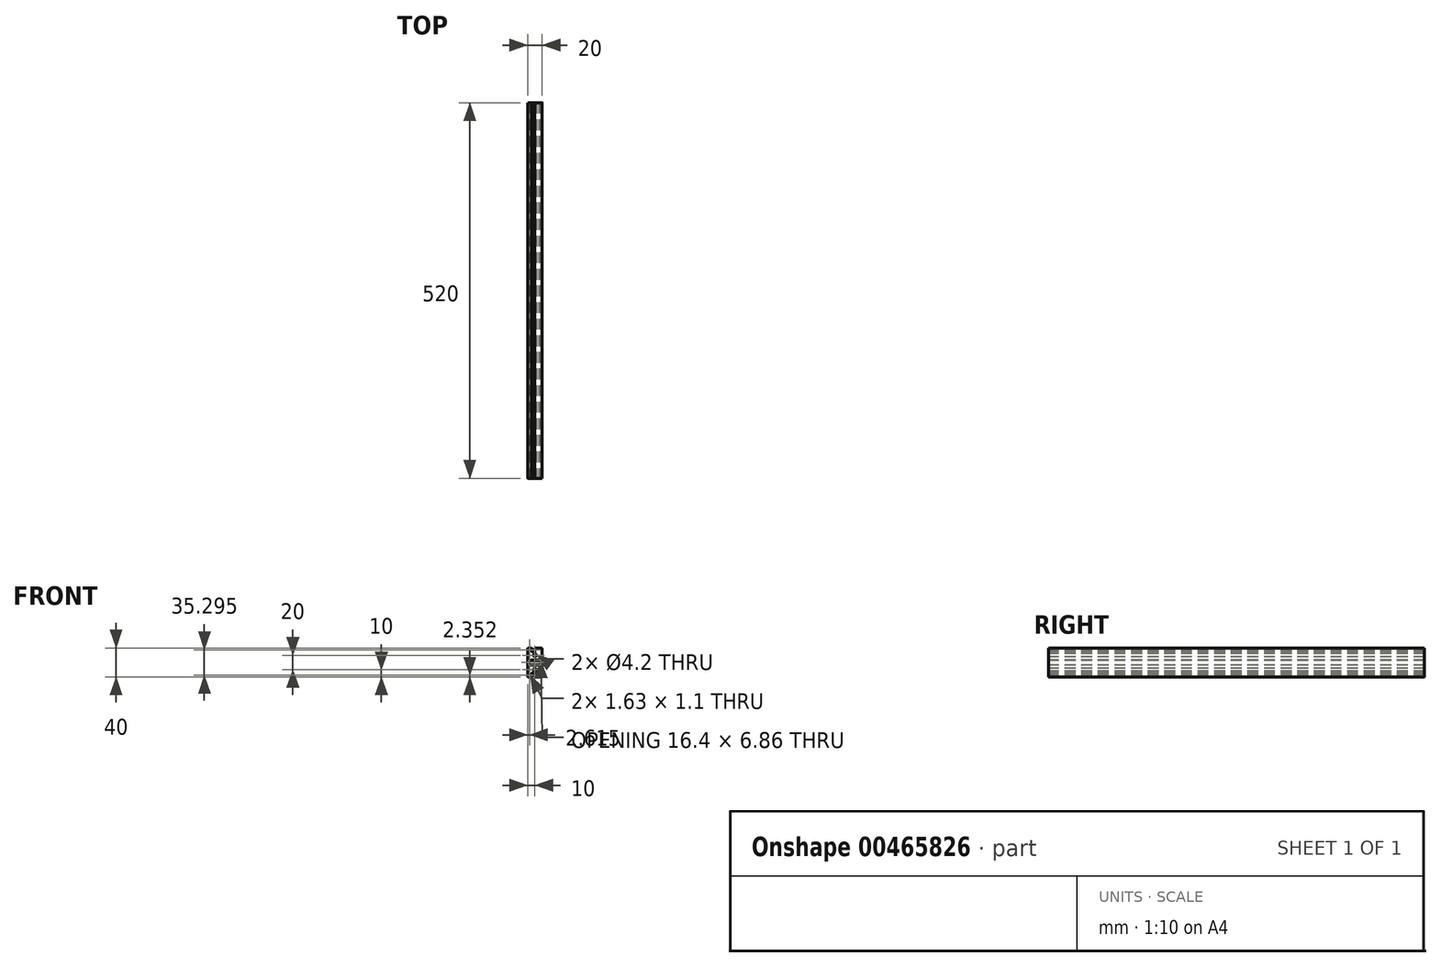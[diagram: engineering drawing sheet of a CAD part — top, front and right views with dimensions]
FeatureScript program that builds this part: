
annotation { "Feature Type Name" : "Feature", "Feature Type Description" : "" }
export const myFeature = defineFeature(function(context is Context, id is Id, definition is map)
    precondition{}
    {
        {
            var Q0;
            Q0=qCreatedBy(makeId("Front.planeOp"),FACE);
            var sketch = newSketch(context, id + "F0", { "sketchPlane" : qUnion([Q0])});
            skLineSegment(sketch, "E0.bottom", {"start": v(10, 10) * mm, "end": v(-10, 10) * mm});
            skLineSegment(sketch, "E0.top", {"start": v(10, -10) * mm, "end": v(-10, -10) * mm});
            skLineSegment(sketch, "E0.left", {"start": v(10, 10) * mm, "end": v(10, -10) * mm});
            skLineSegment(sketch, "E0.right", {"start": v(-10, 10) * mm, "end": v(-10, -10) * mm});
            skPoint(sketch, "E0.middle", {"position": v(0, 0) * mm});
            skSolve(sketch);
        }
        {
            var Q0;
            Q0=qSketchRegion(id+"F0",true);
            extrude(context, id + "F1", {"entities" : qUnion([Q0]), "depth" : 520 * mm});
        }
        {
            var Q0;
            Q0=makeQuery(id+"F1.opExtrude","CAP_FACE",FACE,{"disambiguationData":[OSD([sQuery(id+"F0.wireOp",EDGE,"E0.bottom"),sQuery(id+"F0.wireOp",EDGE,"E0.top"),sQuery(id+"F0.wireOp",EDGE,"E0.left"),sQuery(id+"F0.wireOp",EDGE,"E0.right")])],"isStart":false});
            var sketch = newSketch(context, id + "F2", { "sketchPlane" : qUnion([Q0])});
            skCircle(sketch, "E1", {"center": v(0, 0) * mm, "radius": 2.1 * mm});
            skSolve(sketch);
        }
        {
            var Q0;
            Q0=qSketchRegion(id+"F2",true);
            extrude(context, id + "F3", {"entities" : qUnion([Q0]), "operationType" : NewBodyOperationType.REMOVE, "endBound" : BoundingType.THROUGH_ALL, "oppositeDirection" : true, "depth" : 25 * mm});
        }
        {
            var Q0;
            Q0=makeQuery(id+"F1.opExtrude","SWEPT_EDGE",EDGE,{"disambiguationData":[OSD([sQuery(id+"F0.wireOp",EDGE,"E0.bottom"),sQuery(id+"F0.wireOp",EDGE,"E0.right")])]});
            var Q1;
            Q1=makeQuery(id+"F1.opExtrude","SWEPT_EDGE",EDGE,{"disambiguationData":[OSD([sQuery(id+"F0.wireOp",EDGE,"E0.bottom"),sQuery(id+"F0.wireOp",EDGE,"E0.left")])]});
            var Q2;
            Q2=makeQuery(id+"F1.opExtrude","SWEPT_EDGE",EDGE,{"disambiguationData":[OSD([sQuery(id+"F0.wireOp",EDGE,"E0.top"),sQuery(id+"F0.wireOp",EDGE,"E0.left")])]});
            var Q3;
            Q3=makeQuery(id+"F1.opExtrude","SWEPT_EDGE",EDGE,{"disambiguationData":[OSD([sQuery(id+"F0.wireOp",EDGE,"E0.top"),sQuery(id+"F0.wireOp",EDGE,"E0.right")])]});
            fillet(context, id + "F4", {"entities" : qUnion([Q0, Q1, Q2, Q3]), "radius" : 1 * mm, "tangentPropagation" : true, "allowEdgeOverflow" : false});
        }
        {
            var Q0;
            Q0=makeQuery(id+"F1.opExtrude","CAP_FACE",FACE,{"disambiguationData":[OSD([sQuery(id+"F0.wireOp",EDGE,"E0.bottom"),sQuery(id+"F0.wireOp",EDGE,"E0.top"),sQuery(id+"F0.wireOp",EDGE,"E0.left"),sQuery(id+"F0.wireOp",EDGE,"E0.right")])],"isStart":false});
            var sketch = newSketch(context, id + "F5", { "sketchPlane" : qUnion([Q0])});
            skLineSegment(sketch, "E2", {"start": v(0, 10) * mm, "end": v(-2.84, 10) * mm});
            skLineSegment(sketch, "E3", {"start": v(-2.84, 10) * mm, "end": v(-2.84, 8.2) * mm, "construction": true});
            skLineSegment(sketch, "E4", {"start": v(-2.84, 8.2) * mm, "end": v(-5.5, 8.2) * mm});
            skLineSegment(sketch, "E5", {"start": v(-2.84, 3.9) * mm, "end": v(0, 3.9) * mm});
            skLineSegment(sketch, "E6", {"start": v(0, 3.9) * mm, "end": v(0, 10) * mm});
            skLineSegment(sketch, "E7", {"start": v(-5.5, 8.2) * mm, "end": v(-5.5, 6.56) * mm});
            skLineSegment(sketch, "E8", {"start": v(-5.5, 6.56) * mm, "end": v(-2.84, 3.9) * mm});
            skPoint(sketch, "E9.endSnap0", {"position": v(-1.42, 3.9) * mm});
            skLineSegment(sketch, "E10", {"start": v(0, 0) * mm, "end": v(-9.7, 9.7) * mm, "construction": true});
            skLineSegment(sketch, "E11", {"start": v(-2.84, 8.2) * mm, "end": v(-4.64, 10) * mm});
            skLineSegment(sketch, "E12", {"start": v(-4.64, 10) * mm, "end": v(-2.84, 10) * mm});
            skLineSegment(sketch, "E13", {"start": v(-8.2, 8.2) * mm, "end": v(-6.57, 8.2) * mm});
            skLineSegment(sketch, "E14", {"start": v(-6.57, 8.2) * mm, "end": v(-6.57, 7.62) * mm});
            skLineSegment(sketch, "E15", {"start": v(-6.57, 7.62) * mm, "end": v(-7.1, 7.1) * mm});
            skLineSegment(sketch, "E16", {"start": v(-7.1, 7.1) * mm, "end": v(-8.2, 8.2) * mm});
            skSolve(sketch);
        }
        {
            var Q0;
            Q0=qSketchRegion(id+"F5",true);
            extrude(context, id + "F6", {"entities" : qUnion([Q0]), "operationType" : NewBodyOperationType.REMOVE, "endBound" : BoundingType.THROUGH_ALL, "oppositeDirection" : true, "depth" : 25 * mm});
        }
        {
            var Q0;
            Q0=qCreatedBy(makeId("Top.planeOp"),FACE);
            var sketch = newSketch(context, id + "F7", { "sketchPlane" : qUnion([Q0])});
            skLineSegment(sketch, "E17", {"start": v(0, 0) * mm, "end": v(0, -25.58) * mm, "construction": true});
            skSolve(sketch);
        }
        {
            var Q0;
            Q0=makeQuery(id+"F1.opExtrude","SWEPT_BODY",BODY,{"disambiguationData":[OSD([sQuery(id+"F0.wireOp",EDGE,"E0.bottom"),sQuery(id+"F0.wireOp",EDGE,"E0.top"),sQuery(id+"F0.wireOp",EDGE,"E0.left"),sQuery(id+"F0.wireOp",EDGE,"E0.right")])]});
            var Q1;
            {var subQ2=sQuery(id+"F0.wireOp",EDGE,"E0.top");Q1=makeQuery(id+"FZ8y8MfCgaZ2miL_1.2.F6.boolean.opBoolean","SPLIT",FACE,{"disambiguationData":[TD([makeQuery(id+"FZ8y8MfCgaZ2miL_1.2.F6.opExtrude","SWEPT_FACE",FACE,{"disambiguationData":[OSD([sQuery(id+"F5.wireOp",EDGE,"E11")])]})])],"derivedFrom":makeQuery(id+"F1.opExtrude","SWEPT_FACE",FACE,{"disambiguationData":[OSD([subQ2])]})});}
            mirror(context, id + "F8", {"operationType" : NewBodyOperationType.ADD, "entities" : qUnion([Q0]), "mirrorPlane" : qUnion([Q1])});
        }
        {
            var Q0;
            {var subQ0=makeQuery(id+"F1.opExtrude","CAP_FACE",FACE,{"disambiguationData":[OSD([sQuery(id+"F0.wireOp",EDGE,"E0.bottom"),sQuery(id+"F0.wireOp",EDGE,"E0.top"),sQuery(id+"F0.wireOp",EDGE,"E0.left"),sQuery(id+"F0.wireOp",EDGE,"E0.right")])],"isStart":false});Q0=makeQuery(id+"F8.boolean.opBoolean","MERGE",FACE,{"derivedFrom":[subQ0,makeQuery(id+"F8.opPattern","COPY",FACE,{"derivedFrom":subQ0,"instanceName":"1"})]});}
            var sketch = newSketch(context, id + "F9", { "sketchPlane" : qUnion([Q0])});
            skLineSegment(sketch, "E18.bottom", {"start": v(-8.2, -13.43) * mm, "end": v(8.2, -13.43) * mm});
            skLineSegment(sketch, "E18.top", {"start": v(-8.2, -6.57) * mm, "end": v(8.2, -6.57) * mm});
            skLineSegment(sketch, "E18.left", {"start": v(-8.2, -13.43) * mm, "end": v(-8.2, -6.57) * mm});
            skLineSegment(sketch, "E18.right", {"start": v(8.2, -13.43) * mm, "end": v(8.2, -6.57) * mm});
            skSolve(sketch);
        }
        {
            var Q0;
            Q0=qSketchRegion(id+"F9",true);
            extrude(context, id + "F10", {"entities" : qUnion([Q0]), "operationType" : NewBodyOperationType.REMOVE, "endBound" : BoundingType.THROUGH_ALL, "oppositeDirection" : true, "depth" : 25 * mm});
        }
        {
            var Q0;
            {var subQ0=makeQuery(id+"F1.opExtrude","CAP_FACE",FACE,{"disambiguationData":[OSD([sQuery(id+"F0.wireOp",EDGE,"E0.bottom"),sQuery(id+"F0.wireOp",EDGE,"E0.top"),sQuery(id+"F0.wireOp",EDGE,"E0.left"),sQuery(id+"F0.wireOp",EDGE,"E0.right")])],"isStart":false});Q0=makeQuery(id+"F8.boolean.opBoolean","MERGE",FACE,{"derivedFrom":[subQ0,makeQuery(id+"F8.opPattern","COPY",FACE,{"derivedFrom":subQ0,"instanceName":"1"})]});}
            var sketch = newSketch(context, id + "F11", { "sketchPlane" : qUnion([Q0])});
            skArc(sketch, "E19.0", {"start": v(-10, -9) * mm, "mid": v(-9.7, -9.7) * mm, "end": v(-9, -10) * mm});
            skArc(sketch, "E19.1", {"start": v(-10, -11) * mm, "mid": v(-9.7, -10.3) * mm, "end": v(-9, -10) * mm});
            skArc(sketch, "E19.2", {"start": v(9, -10) * mm, "mid": v(9.7, -10.3) * mm, "end": v(10, -11) * mm});
            skArc(sketch, "E19.3", {"start": v(9, -10) * mm, "mid": v(9.7, -9.7) * mm, "end": v(10, -9) * mm});
            skLineSegment(sketch, "E20", {"start": v(-10, -9) * mm, "end": v(-10, -11) * mm});
            skLineSegment(sketch, "E21", {"start": v(10, -9) * mm, "end": v(10, -11) * mm});
            skLineSegment(sketch, "E22", {"start": v(8.2, -7) * mm, "end": v(5.94, -7) * mm});
            skLineSegment(sketch, "E23", {"start": v(-8.2, -7) * mm, "end": v(-5.94, -7) * mm});
            skLineSegment(sketch, "E24", {"start": v(-5.5, -6.56) * mm, "end": v(-5.94, -7) * mm});
            skLineSegment(sketch, "E25", {"start": v(5.5, -6.56) * mm, "end": v(5.94, -7) * mm});
            skLineSegment(sketch, "E26.0", {"start": v(8.2, -6.57) * mm, "end": v(5.5, -6.57) * mm});
            skLineSegment(sketch, "E27.0", {"start": v(8.2, -7) * mm, "end": v(8.2, -6.57) * mm});
            skLineSegment(sketch, "E28.0", {"start": v(-8.2, -7) * mm, "end": v(-8.2, -6.57) * mm});
            skLineSegment(sketch, "E29.0", {"start": v(-8.2, -6.57) * mm, "end": v(-5.5, -6.57) * mm});
            skPoint(sketch, "E30.orphan", {"position": v(8.2, -13.43) * mm});
            skPoint(sketch, "E31.orphan", {"position": v(-8.2, -13.43) * mm});
            skSolve(sketch);
        }
        {
            var Q0;
            Q0=qSketchRegion(id+"F11",true);
            var Q1;
            {var subQ0=makeQuery(id+"F1.opExtrude","CAP_FACE",FACE,{"disambiguationData":[OSD([sQuery(id+"F0.wireOp",EDGE,"E0.bottom"),sQuery(id+"F0.wireOp",EDGE,"E0.top"),sQuery(id+"F0.wireOp",EDGE,"E0.left"),sQuery(id+"F0.wireOp",EDGE,"E0.right")])],"isStart":true});Q1=makeQuery(id+"F8.boolean.opBoolean","MERGE",FACE,{"derivedFrom":[subQ0,makeQuery(id+"F8.opPattern","COPY",FACE,{"derivedFrom":subQ0,"instanceName":"1"})]});}
            extrude(context, id + "F12", {"entities" : qUnion([Q0]), "operationType" : NewBodyOperationType.ADD, "endBound" : BoundingType.UP_TO_SURFACE, "oppositeDirection" : true, "endBoundEntityFace" : qUnion([Q1]), "depth" : 25 * mm});
        }
    });
